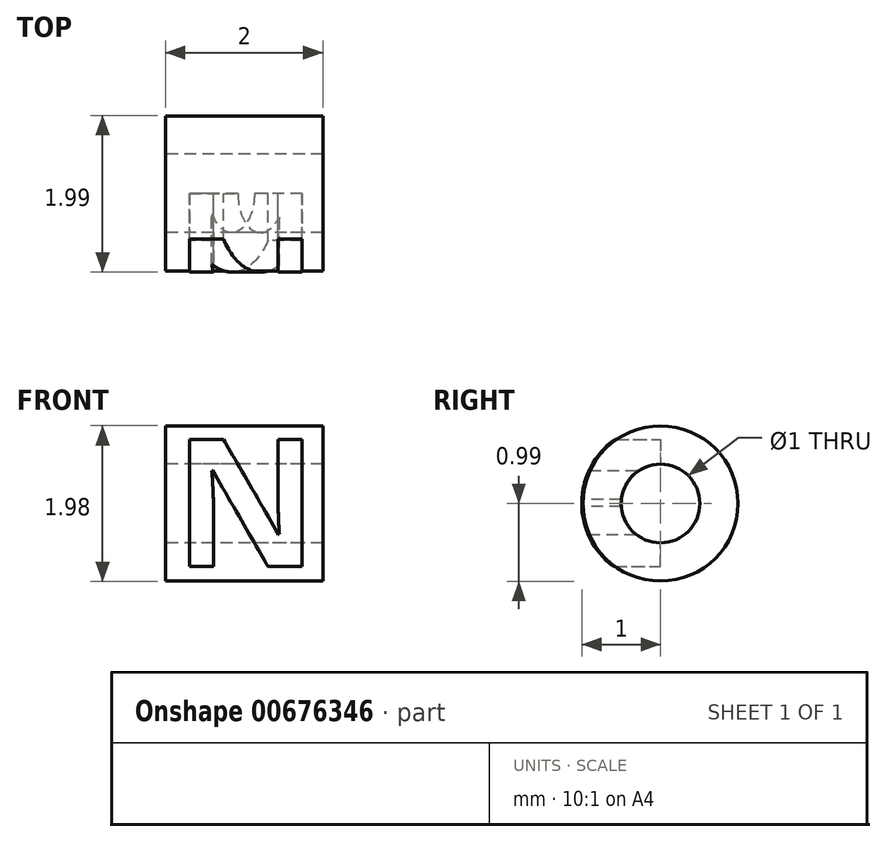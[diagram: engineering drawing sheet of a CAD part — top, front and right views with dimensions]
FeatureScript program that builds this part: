
annotation { "Feature Type Name" : "Feature", "Feature Type Description" : "" }
export const myFeature = defineFeature(function(context is Context, id is Id, definition is map)
    precondition{}
    {
        {
            var Q0;
            Q0=qCreatedBy(makeId("Right.planeOp"),FACE);
            var sketch = newSketch(context, id + "F0", { "sketchPlane" : qUnion([Q0])});
            skCircle(sketch, "E0", {"center": v(0, 0) * mm, "radius": 0.5 * mm});
            skCircle(sketch, "E1", {"center": v(0, 0) * mm, "radius": 1 * mm});
            skCircle(sketch, "E2", {"center": v(0, 0) * mm, "radius": 0.98 * mm});
            skSolve(sketch);
        }
        {
            var Q0;
            Q0=makeQuery(id+"F0.imprint","IMPRINT",FACE,{"disambiguationData":[TD([[makeQuery(id+"F0.imprint","IMPRINT",EDGE,{"derivedFrom":sQuery(id+"F0.wireOp",EDGE,"E0")}),-1.0]])]});
            var Q1;
            Q1=makeQuery(id+"F0.imprint","IMPRINT",FACE,{"disambiguationData":[TD([[makeQuery(id+"F0.imprint","IMPRINT",EDGE,{"derivedFrom":sQuery(id+"F0.wireOp",EDGE,"E1")}),1.0]])]});
            extrude(context, id + "F1", {"entities" : qUnion([Q0, Q1]), "depth" : 2 * mm, "offsetDistance" : 25 * mm});
        }
        {
            var Q0;
            Q0=qCreatedBy(makeId("Front.planeOp"),FACE);
            var sketch = newSketch(context, id + "F2", { "sketchPlane" : qUnion([Q0])});
            skText(sketch, "E3", { "text": "N", "fontName": "OpenSans-Bold.ttf"});
            const initialGuessF2  = {"E3": [0.0001, -0.0008, 1, 0, 0.00163]};
            skSetInitialGuess(sketch, initialGuessF2);
            skSolve(sketch);
        }
        {
            var Q0;
            Q0=qSketchRegion(id+"F2",true);
            var Q1;
            Q1=qConstructionFilter(qBodyType(qCreatedBy(id+"F2",EDGE),BodyType.WIRE),ConstructionObject.NO);
            var Q2;
            Q2=makeQuery(id+"F1.opExtrude","SWEPT_FACE",FACE,{"disambiguationData":[OSD([sQuery(id+"F0.wireOp",EDGE,"E1")])]});
            var Q3;
            Q3=makeQuery(id+"F1.opExtrude","SWEPT_BODY",BODY,{"disambiguationData":[OSD([sQuery(id+"F0.wireOp",EDGE,"E0"),sQuery(id+"F0.wireOp",EDGE,"E1")])]});
            var Q4;
            Q4=sQuery(id+"F0.wireOp",VERTEX,"27635d6e-dcd6-4653-b727-4819003c0945");
            extrude(context, id + "F3", {"entities" : qUnion([Q0]), "operationType" : NewBodyOperationType.INTERSECT, "surfaceEntities" : qUnion([Q1]), "endBound" : BoundingType.UP_TO_SURFACE, "endBoundEntityFace" : qUnion([Q2]), "endBoundEntityBody" : qUnion([Q3]), "endBoundEntityVertex" : qUnion([Q4]), "depth" : 25 * mm, "offsetDistance" : 25 * mm});
        }
        {
            var Q0;
            Q0=makeQuery(id+"F0.imprint","IMPRINT",FACE,{"disambiguationData":[TD([[makeQuery(id+"F0.imprint","IMPRINT",EDGE,{"derivedFrom":sQuery(id+"F0.wireOp",EDGE,"E0")}),-1.0]])]});
            extrude(context, id + "F4", {"entities" : qUnion([Q0]), "depth" : 2 * mm, "offsetDistance" : 25 * mm});
        }
    });
